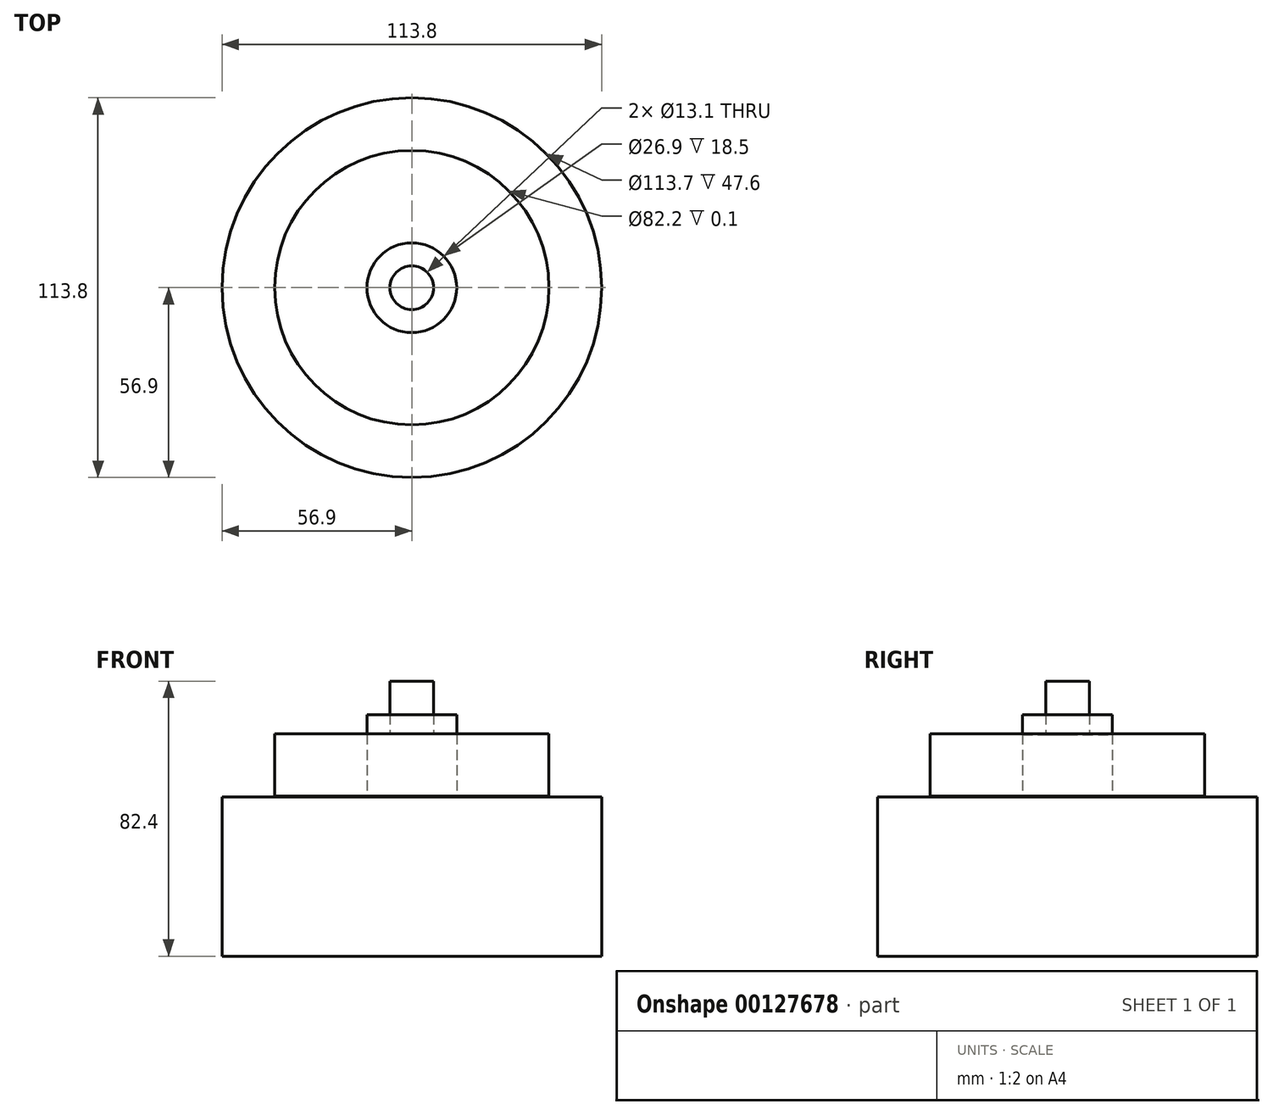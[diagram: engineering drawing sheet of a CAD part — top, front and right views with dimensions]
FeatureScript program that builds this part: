
annotation { "Feature Type Name" : "Feature", "Feature Type Description" : "" }
export const myFeature = defineFeature(function(context is Context, id is Id, definition is map)
    precondition{}
    {
        {
            var Q0;
            Q0=qCreatedBy(makeId("Top.planeOp"),FACE);
            var sketch = newSketch(context, id + "F0", { "sketchPlane" : qUnion([Q0])});
            skCircle(sketch, "E0", {"center": v(0, 0) * mm, "radius": 56.9 * mm});
            skSolve(sketch);
        }
        {
            var Q0;
            Q0=makeQuery(id+"F0.imprint","IMPRINT",FACE,{"disambiguationData":[TD([[makeQuery(id+"F0.imprint","IMPRINT",EDGE,{"derivedFrom":sQuery(id+"F0.wireOp",EDGE,"E0")}),1.0]])]});
            extrude(context, id + "F1", {"entities" : qUnion([Q0]), "depth" : 47.7 * mm});
        }
        {
            var Q0;
            Q0=qCreatedBy(makeId("Top.planeOp"),FACE);
            var sketch = newSketch(context, id + "F2", { "sketchPlane" : qUnion([Q0])});
            skCircle(sketch, "E1", {"center": v(0, 0) * mm, "radius": 56.85 * mm});
            skSolve(sketch);
        }
        {
            var Q0;
            Q0 = qSketchRegion(id + "F2", true);
            extrude(context, id + "F3", {"entities" : qUnion([Q0]), "operationType" : NewBodyOperationType.REMOVE, "depth" : 47.6 * mm});
        }
        {
            var Q0;
            Q0=qCreatedBy(makeId("Top.planeOp"),FACE);
            var sketch = newSketch(context, id + "F4", { "sketchPlane" : qUnion([Q0])});
            skCircle(sketch, "E2", {"center": v(0, 0) * mm, "radius": 41.1 * mm});
            skSolve(sketch);
        }
        {
            var Q0;
            Q0 = qSketchRegion(id + "F4", true);
            extrude(context, id + "F5", {"entities" : qUnion([Q0]), "operationType" : NewBodyOperationType.ADD, "depth" : 66.6 * mm});
        }
        {
            var Q0;
            Q0 = qSketchRegion(id + "F4", true);
            extrude(context, id + "F6", {"entities" : qUnion([Q0]), "operationType" : NewBodyOperationType.REMOVE, "depth" : 47.9 * mm});
        }
        {
            var Q0;
            Q0=qCreatedBy(makeId("Top.planeOp"),FACE);
            var sketch = newSketch(context, id + "F7", { "sketchPlane" : qUnion([Q0])});
            skCircle(sketch, "E3", {"center": v(0, 0) * mm, "radius": 13.45 * mm});
            skSolve(sketch);
        }
        {
            var Q0;
            Q0 = qSketchRegion(id + "F7", true);
            extrude(context, id + "F8", {"entities" : qUnion([Q0]), "depth" : 72.4 * mm});
        }
        {
            var Q0;
            Q0 = qSketchRegion(id + "F7", true);
            extrude(context, id + "F9", {"entities" : qUnion([Q0]), "operationType" : NewBodyOperationType.REMOVE, "depth" : 66.4 * mm});
        }
        {
            var Q0;
            Q0=qCreatedBy(makeId("Top.planeOp"),FACE);
            var sketch = newSketch(context, id + "F10", { "sketchPlane" : qUnion([Q0])});
            skCircle(sketch, "E4", {"center": v(0, 0) * mm, "radius": 6.55 * mm});
            skSolve(sketch);
        }
        {
            var Q0;
            Q0 = qSketchRegion(id + "F10", true);
            extrude(context, id + "F11", {"entities" : qUnion([Q0]), "depth" : 82.4 * mm});
        }
        {
            var Q0;
            Q0 = qSketchRegion(id + "F10", true);
            extrude(context, id + "F12", {"entities" : qUnion([Q0]), "operationType" : NewBodyOperationType.REMOVE, "depth" : 72.4 * mm});
        }
    });
